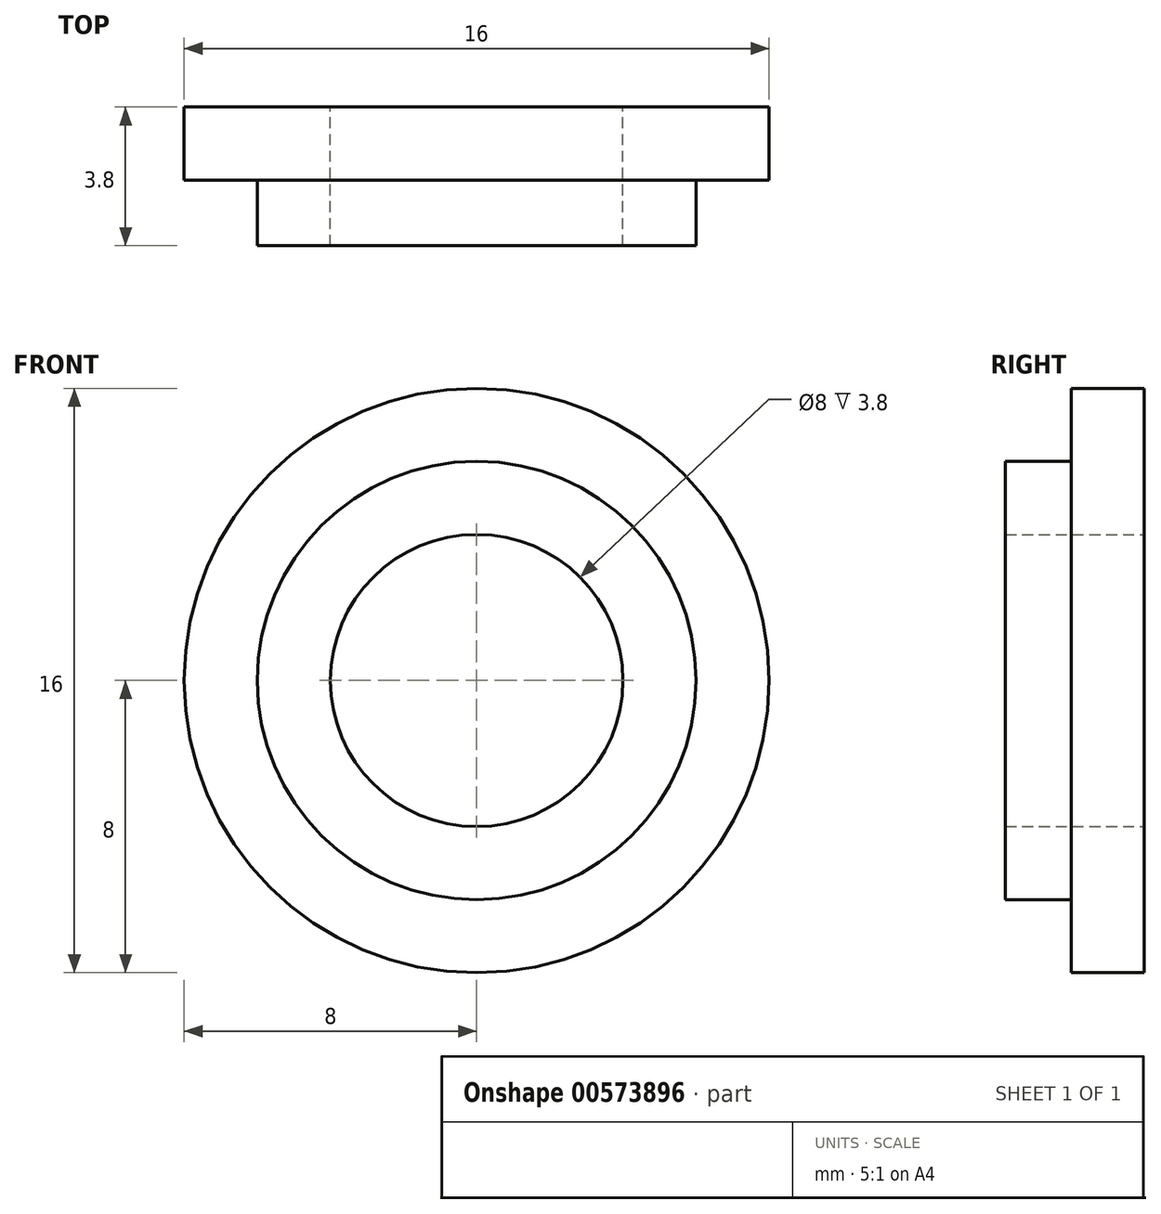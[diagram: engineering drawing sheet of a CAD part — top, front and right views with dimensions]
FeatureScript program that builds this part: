
annotation { "Feature Type Name" : "Feature", "Feature Type Description" : "" }
export const myFeature = defineFeature(function(context is Context, id is Id, definition is map)
    precondition{}
    {
        {
            var Q0;
            Q0=qCreatedBy(makeId("Front.planeOp"),FACE);
            var sketch = newSketch(context, id + "F0", { "sketchPlane" : qUnion([Q0])});
            skCircle(sketch, "E0", {"center": v(0, 0) * mm, "radius": 4 * mm});
            skCircle(sketch, "E1", {"center": v(0, 0) * mm, "radius": 6 * mm});
            skCircle(sketch, "E2", {"center": v(0, 0) * mm, "radius": 8 * mm});
            skCircle(sketch, "E3", {"center": v(0, 0) * mm, "radius": 13.37 * mm});
            skLineSegment(sketch, "E4", {"start": v(-4.92, -3.43) * mm, "end": v(4.92, -3.43) * mm});
            skSolve(sketch);
        }
        {
            var Q0;
            Q0=makeQuery(id+"F0.imprint","IMPRINT",FACE,{"disambiguationData":[TD([[makeQuery(id+"F0.imprint","IMPRINT",EDGE,{"derivedFrom":sQuery(id+"F0.wireOp",EDGE,"E0")}),-1.0]])]});
            extrude(context, id + "F1", {"entities" : qUnion([Q0]), "depth" : 3.8 * mm, "offsetDistance" : 25 * mm});
        }
        {
            var Q0;
            Q0=makeQuery(id+"F0.imprint","IMPRINT",FACE,{"disambiguationData":[TD([[makeQuery(id+"F0.imprint","IMPRINT",EDGE,{"derivedFrom":sQuery(id+"F0.wireOp",EDGE,"E1")}),-1.0]])]});
            var Q1;
            {var subQ0=sQuery(id+"F0.wireOp",EDGE,"E4");var subQ1=sQuery(id+"F0.wireOp",EDGE,"E0");var subQ2=makeQuery(id+"F0.imprint","INTERSECT",VERTEX,{"disambiguationData":[OD(0.0)],"derivedFrom":[subQ1,subQ0]});Q1=makeQuery(id+"F0.imprint","IMPRINT",FACE,{"disambiguationData":[TD([[makeQuery(id+"F0.imprint","IMPRINT",EDGE,{"disambiguationData":[TD([[subQ2,-1.0]])],"derivedFrom":subQ1}),-1.0]])]});}
            var Q2;
            {var subQ0=sQuery(id+"F0.wireOp",EDGE,"E4");var subQ1=sQuery(id+"F0.wireOp",EDGE,"E0");var subQ2=makeQuery(id+"F0.imprint","INTERSECT",VERTEX,{"disambiguationData":[OD(0.0)],"derivedFrom":[subQ1,subQ0]});Q2=makeQuery(id+"F0.imprint","IMPRINT",FACE,{"disambiguationData":[TD([[makeQuery(id+"F0.imprint","IMPRINT",EDGE,{"disambiguationData":[TD([[subQ2,1.0]])],"derivedFrom":subQ1}),-1.0]])]});}
            extrude(context, id + "F2", {"entities" : qUnion([Q0, Q1, Q2]), "operationType" : NewBodyOperationType.ADD, "depth" : 2 * mm, "offsetDistance" : 25 * mm});
        }
    });
